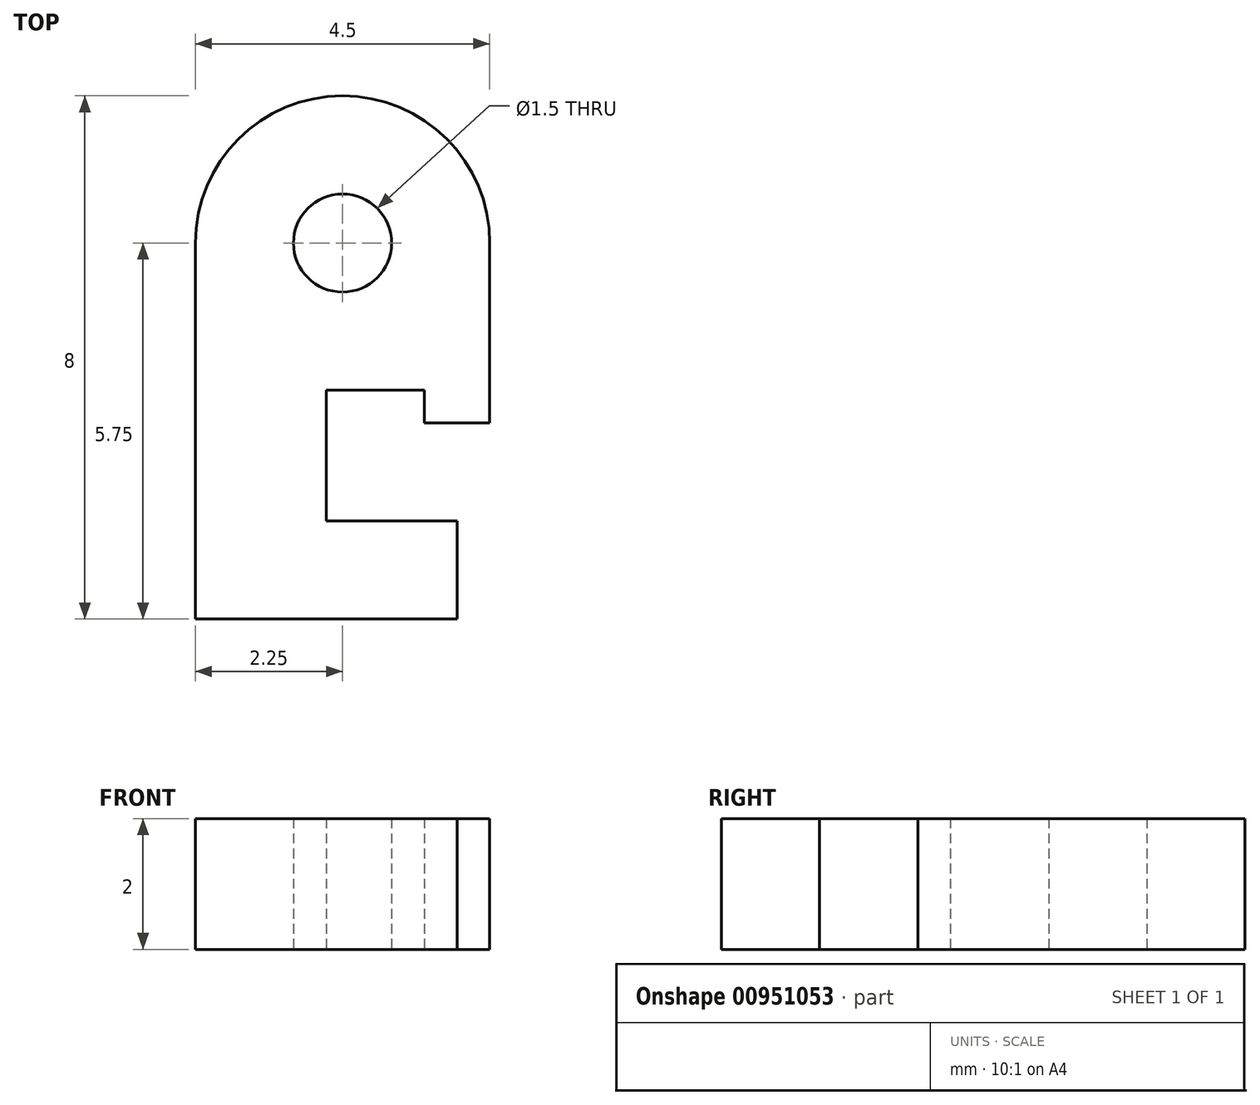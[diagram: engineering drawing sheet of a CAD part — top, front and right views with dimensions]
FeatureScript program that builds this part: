
annotation { "Feature Type Name" : "Feature", "Feature Type Description" : "" }
export const myFeature = defineFeature(function(context is Context, id is Id, definition is map)
    precondition{}
    {
        {
            var Q0;
            Q0=qCreatedBy(makeId("Top.planeOp"),FACE);
            var sketch = newSketch(context, id + "F0", { "sketchPlane" : qUnion([Q0])});
            skLineSegment(sketch, "E0.bottom", {"start": v(3.5, 3) * mm, "end": v(4.5, 3) * mm});
            skLineSegment(sketch, "E0.top", {"start": v(2, 1.5) * mm, "end": v(4, 1.5) * mm});
            skLineSegment(sketch, "E0.left", {"start": v(2, 3) * mm, "end": v(2, 1.5) * mm});
            skLineSegment(sketch, "E1", {"start": v(0, 8) * mm, "end": v(0, 0) * mm});
            skLineSegment(sketch, "E2", {"start": v(0, 0) * mm, "end": v(4, 0) * mm});
            skLineSegment(sketch, "E3", {"start": v(4, 0) * mm, "end": v(4, 1.5) * mm});
            skLineSegment(sketch, "E4", {"start": v(4.5, 3) * mm, "end": v(4.5, 5.75) * mm});
            skLineSegment(sketch, "E5", {"start": v(2.25, 8) * mm, "end": v(2.25, 8) * mm});
            skLineSegment(sketch, "E6", {"start": v(3.5, 3) * mm, "end": v(3.5, 3.5) * mm});
            skLineSegment(sketch, "E7", {"start": v(3.5, 3.5) * mm, "end": v(2, 3.5) * mm});
            skLineSegment(sketch, "E8", {"start": v(2, 3.5) * mm, "end": v(2, 3) * mm});
            skLineSegment(sketch, "E9", {"start": v(0, 5.75) * mm, "end": v(0, 0) * mm});
            skPoint(sketch, "E10.visualSharp", {"position": v(0, 8) * mm});
            skArc(sketch, "E10.filletArc", {"start": v(2.25, 8) * mm, "mid": v(0.66, 7.34) * mm, "end": v(0, 5.75) * mm});
            skPoint(sketch, "E11.visualSharp", {"position": v(4.5, 8) * mm});
            skArc(sketch, "E11.filletArc", {"start": v(4.5, 5.75) * mm, "mid": v(3.84, 7.34) * mm, "end": v(2.25, 8) * mm});
            skCircle(sketch, "E12", {"center": v(2.25, 5.75) * mm, "radius": 0.75 * mm});
            skSolve(sketch);
        }
        {
            var Q0;
            Q0 = qSketchRegion(id + "F0", true);
            extrude(context, id + "F1", {"entities" : qUnion([Q0]), "depth" : 2 * mm, "offsetDistance" : 25 * mm});
        }
    });
